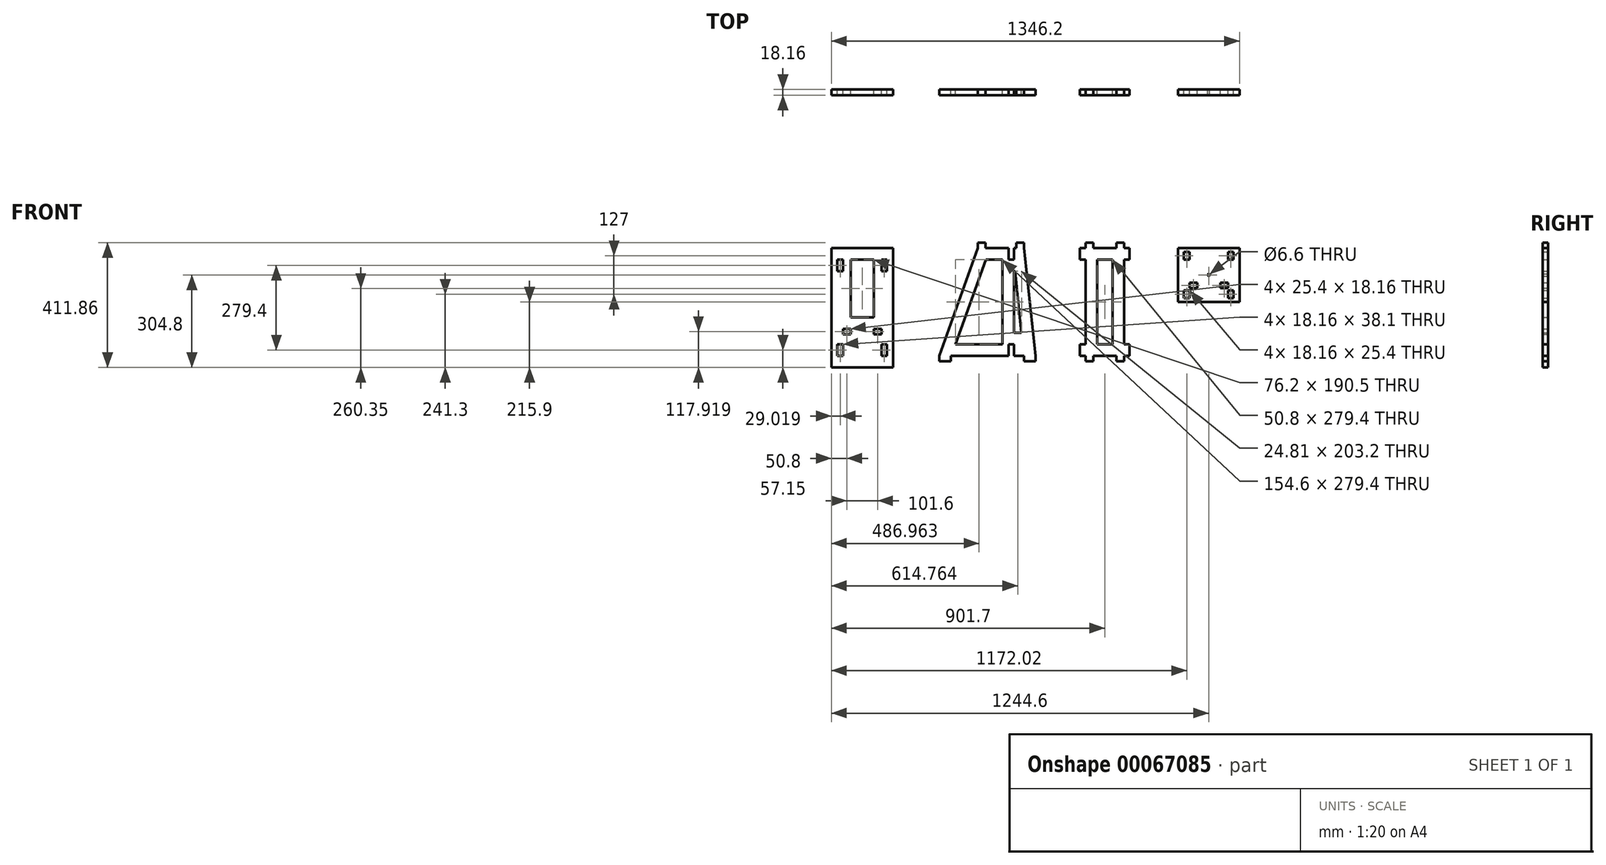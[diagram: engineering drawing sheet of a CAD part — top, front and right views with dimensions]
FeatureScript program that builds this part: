
annotation { "Feature Type Name" : "Feature", "Feature Type Description" : "" }
export const myFeature = defineFeature(function(context is Context, id is Id, definition is map)
    precondition{}
    {
        {
            var Q0;
            Q0=qCreatedBy(makeId("Front.planeOp"),FACE);
            var sketch = newSketch(context, id + "F0", { "sketchPlane" : qUnion([Q0])});
            skLineSegment(sketch, "E0", {"start": v(0, 177.8) * mm, "end": v(0, 139.7) * mm});
            skLineSegment(sketch, "E1.0", {"start": v(18.16, 177.8) * mm, "end": v(18.16, 139.7) * mm});
            skLineSegment(sketch, "E2", {"start": v(0, 177.8) * mm, "end": v(-76.2, 177.8) * mm});
            skLineSegment(sketch, "E3", {"start": v(18.16, 177.8) * mm, "end": v(25.4, 177.8) * mm});
            skLineSegment(sketch, "E4", {"start": v(0, -177.8) * mm, "end": v(-190.5, -177.8) * mm});
            skLineSegment(sketch, "E5", {"start": v(18.16, -177.8) * mm, "end": v(50.8, -177.8) * mm});
            skLineSegment(sketch, "E6", {"start": v(-101.6, 177.8) * mm, "end": v(-228.6, -177.8) * mm});
            skLineSegment(sketch, "E7", {"start": v(50.8, 177.8) * mm, "end": v(88.9, -177.8) * mm});
            skLineSegment(sketch, "E8.0", {"start": v(-19.94, 139.7) * mm, "end": v(-19.94, -139.7) * mm});
            skLineSegment(sketch, "E8.1", {"start": v(-19.94, 139.7) * mm, "end": v(-74.75, 139.7) * mm});
            skLineSegment(sketch, "E8.2", {"start": v(-74.75, 139.7) * mm, "end": v(-174.54, -139.7) * mm});
            skLineSegment(sketch, "E8.3", {"start": v(-19.94, -139.7) * mm, "end": v(-174.54, -139.7) * mm});
            skLineSegment(sketch, "E9", {"start": v(0, 139.7) * mm, "end": v(18.16, 139.7) * mm});
            skLineSegment(sketch, "E10", {"start": v(0, -139.7) * mm, "end": v(18.16, -139.7) * mm});
            skLineSegment(sketch, "E11.top", {"start": v(-101.6, 195.96) * mm, "end": v(-76.2, 195.96) * mm});
            skLineSegment(sketch, "E11.left", {"start": v(-101.6, 177.8) * mm, "end": v(-101.6, 195.96) * mm});
            skLineSegment(sketch, "E11.right", {"start": v(-76.2, 177.8) * mm, "end": v(-76.2, 195.96) * mm});
            skLineSegment(sketch, "E12.top", {"start": v(50.8, 195.96) * mm, "end": v(25.4, 195.96) * mm});
            skLineSegment(sketch, "E12.left", {"start": v(50.8, 177.8) * mm, "end": v(50.8, 195.96) * mm});
            skLineSegment(sketch, "E12.right", {"start": v(25.4, 177.8) * mm, "end": v(25.4, 195.96) * mm});
            skLineSegment(sketch, "E13.top", {"start": v(-228.6, -195.96) * mm, "end": v(-190.5, -195.96) * mm});
            skLineSegment(sketch, "E13.left", {"start": v(-228.6, -177.8) * mm, "end": v(-228.6, -195.96) * mm});
            skLineSegment(sketch, "E13.right", {"start": v(-190.5, -177.8) * mm, "end": v(-190.5, -195.96) * mm});
            skLineSegment(sketch, "E14.top", {"start": v(88.9, -195.96) * mm, "end": v(50.8, -195.96) * mm});
            skLineSegment(sketch, "E14.left", {"start": v(88.9, -177.8) * mm, "end": v(88.9, -195.96) * mm});
            skLineSegment(sketch, "E14.right", {"start": v(50.8, -177.8) * mm, "end": v(50.8, -195.96) * mm});
            skLineSegment(sketch, "E15", {"start": v(0, 139.7) * mm, "end": v(0, -139.7) * mm, "construction": true});
            skLineSegment(sketch, "E16", {"start": v(18.16, 139.7) * mm, "end": v(18.16, -139.7) * mm, "construction": true});
            skLineSegment(sketch, "E17", {"start": v(0, -139.7) * mm, "end": v(0, -177.8) * mm});
            skLineSegment(sketch, "E18", {"start": v(18.16, -139.7) * mm, "end": v(18.16, -177.8) * mm});
            skLineSegment(sketch, "E19.bottom", {"start": v(279.4, 177.8) * mm, "end": v(355.6, 177.8) * mm});
            skLineSegment(sketch, "E19.top", {"start": v(279.4, -177.8) * mm, "end": v(355.6, -177.8) * mm});
            skLineSegment(sketch, "E19.left", {"start": v(254, 139.7) * mm, "end": v(254, -139.7) * mm});
            skLineSegment(sketch, "E19.right", {"start": v(381, 139.7) * mm, "end": v(381, -139.7) * mm});
            skLineSegment(sketch, "E20.bottom", {"start": v(254, 177.8) * mm, "end": v(235.97, 177.8) * mm});
            skLineSegment(sketch, "E20.top", {"start": v(254, 139.7) * mm, "end": v(235.97, 139.7) * mm});
            skLineSegment(sketch, "E20.right", {"start": v(235.97, 177.8) * mm, "end": v(235.97, 139.7) * mm});
            skLineSegment(sketch, "E21", {"start": v(317.5, 177.8) * mm, "end": v(317.5, -177.8) * mm, "construction": true});
            skLineSegment(sketch, "E22", {"start": v(317.5, -177.8) * mm, "end": v(381, 0) * mm, "construction": true});
            skLineSegment(sketch, "E23", {"start": v(381, 0) * mm, "end": v(254, 0) * mm, "construction": true});
            skLineSegment(sketch, "E24.MirrorCS", {"start": v(381, 177.8) * mm, "end": v(399.03, 177.8) * mm});
            skLineSegment(sketch, "E25.MirrorCS", {"start": v(399.03, 177.8) * mm, "end": v(399.03, 139.7) * mm});
            skLineSegment(sketch, "E26.MirrorCS", {"start": v(381, 139.7) * mm, "end": v(399.03, 139.7) * mm});
            skLineSegment(sketch, "E27.MirrorCS", {"start": v(254, -177.8) * mm, "end": v(235.97, -177.8) * mm});
            skLineSegment(sketch, "E28.MirrorCS", {"start": v(381, -139.7) * mm, "end": v(399.03, -139.7) * mm});
            skLineSegment(sketch, "E29.MirrorCS", {"start": v(381, -177.8) * mm, "end": v(399.03, -177.8) * mm});
            skLineSegment(sketch, "E30.MirrorCS", {"start": v(254, -139.7) * mm, "end": v(235.97, -139.7) * mm});
            skLineSegment(sketch, "E31.MirrorCS", {"start": v(235.97, -177.8) * mm, "end": v(235.97, -139.7) * mm});
            skLineSegment(sketch, "E32.MirrorCS", {"start": v(399.03, -177.8) * mm, "end": v(399.03, -139.7) * mm});
            skLineSegment(sketch, "E33.top", {"start": v(254, -195.96) * mm, "end": v(279.4, -195.96) * mm});
            skLineSegment(sketch, "E33.left", {"start": v(254, -177.8) * mm, "end": v(254, -195.96) * mm});
            skLineSegment(sketch, "E33.right", {"start": v(279.4, -177.8) * mm, "end": v(279.4, -195.96) * mm});
            skLineSegment(sketch, "E34.MirrorCS", {"start": v(381, -195.96) * mm, "end": v(355.6, -195.96) * mm});
            skLineSegment(sketch, "E35.MirrorCS", {"start": v(381, -177.8) * mm, "end": v(381, -195.96) * mm});
            skLineSegment(sketch, "E36.MirrorCS", {"start": v(355.6, -177.8) * mm, "end": v(355.6, -195.96) * mm});
            skLineSegment(sketch, "E37.MirrorCS", {"start": v(254, 195.96) * mm, "end": v(279.4, 195.96) * mm});
            skLineSegment(sketch, "E38.MirrorCS", {"start": v(254, 177.8) * mm, "end": v(254, 195.96) * mm});
            skLineSegment(sketch, "E39.MirrorCS", {"start": v(279.4, 177.8) * mm, "end": v(279.4, 195.96) * mm});
            skLineSegment(sketch, "E40.MirrorCS", {"start": v(355.6, 177.8) * mm, "end": v(355.6, 195.96) * mm});
            skLineSegment(sketch, "E41.MirrorCS", {"start": v(381, 177.8) * mm, "end": v(381, 195.96) * mm});
            skLineSegment(sketch, "E42.MirrorCS", {"start": v(381, 195.96) * mm, "end": v(355.6, 195.96) * mm});
            skPoint(sketch, "E43.orphan", {"position": v(381, -177.8) * mm});
            skPoint(sketch, "E44.orphan", {"position": v(381, 177.8) * mm});
            skLineSegment(sketch, "E45.0", {"start": v(292.1, 139.7) * mm, "end": v(342.9, 139.7) * mm});
            skLineSegment(sketch, "E46.0", {"start": v(342.9, 139.7) * mm, "end": v(342.9, -139.7) * mm});
            skLineSegment(sketch, "E47.0", {"start": v(292.1, 139.7) * mm, "end": v(292.1, -139.7) * mm});
            skLineSegment(sketch, "E48.0", {"start": v(292.1, -139.7) * mm, "end": v(342.9, -139.7) * mm});
            skLineSegment(sketch, "E49", {"start": v(22.08, 101.6) * mm, "end": v(42.97, -101.6) * mm});
            skLineSegment(sketch, "E50.0", {"start": v(18.16, 101.6) * mm, "end": v(22.08, 101.6) * mm});
            skLineSegment(sketch, "E51.0", {"start": v(18.16, -101.6) * mm, "end": v(42.97, -101.6) * mm});
            skLineSegment(sketch, "E52", {"start": v(18.16, 101.6) * mm, "end": v(18.16, -101.6) * mm});
            skLineSegment(sketch, "E53.bottom", {"start": v(558.8, 177.8) * mm, "end": v(762, 177.8) * mm});
            skLineSegment(sketch, "E53.top", {"start": v(558.8, 0) * mm, "end": v(762, 0) * mm});
            skLineSegment(sketch, "E53.left", {"start": v(558.8, 177.8) * mm, "end": v(558.8, 0) * mm});
            skLineSegment(sketch, "E53.right", {"start": v(762, 177.8) * mm, "end": v(762, 0) * mm});
            skLineSegment(sketch, "E54", {"start": v(558.8, 88.9) * mm, "end": v(762, 88.9) * mm, "construction": true});
            skLineSegment(sketch, "E55", {"start": v(762, 88.9) * mm, "end": v(660.4, 177.8) * mm, "construction": true});
            skLineSegment(sketch, "E56", {"start": v(660.4, 177.8) * mm, "end": v(660.4, 0) * mm, "construction": true});
            skLineSegment(sketch, "E57.0", {"start": v(596.9, 177.8) * mm, "end": v(596.9, 0) * mm, "construction": true});
            skLineSegment(sketch, "E58.0", {"start": v(723.9, 177.8) * mm, "end": v(723.9, 0) * mm, "construction": true});
            skLineSegment(sketch, "E59.0", {"start": v(558.8, 12.7) * mm, "end": v(762, 12.7) * mm, "construction": true});
            skLineSegment(sketch, "E60.0", {"start": v(558.8, 165.1) * mm, "end": v(762, 165.1) * mm, "construction": true});
            skLineSegment(sketch, "E61.0", {"start": v(558.8, 63.5) * mm, "end": v(762, 63.5) * mm, "construction": true});
            skLineSegment(sketch, "E62.bottom", {"start": v(596.9, 63.5) * mm, "end": v(622.3, 63.5) * mm});
            skLineSegment(sketch, "E62.top", {"start": v(596.9, 45.34) * mm, "end": v(622.3, 45.34) * mm});
            skLineSegment(sketch, "E62.left", {"start": v(596.9, 63.5) * mm, "end": v(596.9, 45.34) * mm});
            skLineSegment(sketch, "E62.right", {"start": v(622.3, 63.5) * mm, "end": v(622.3, 45.34) * mm});
            skLineSegment(sketch, "E63.bottom", {"start": v(596.9, 12.7) * mm, "end": v(578.74, 12.7) * mm});
            skLineSegment(sketch, "E63.top", {"start": v(596.9, 38.1) * mm, "end": v(578.74, 38.1) * mm});
            skLineSegment(sketch, "E63.left", {"start": v(596.9, 12.7) * mm, "end": v(596.9, 38.1) * mm});
            skLineSegment(sketch, "E63.right", {"start": v(578.74, 12.7) * mm, "end": v(578.74, 38.1) * mm});
            skLineSegment(sketch, "E64.MirrorCS", {"start": v(698.5, 63.5) * mm, "end": v(698.5, 45.34) * mm});
            skLineSegment(sketch, "E65.MirrorCS", {"start": v(723.9, 63.5) * mm, "end": v(723.9, 45.34) * mm});
            skLineSegment(sketch, "E66.MirrorCS", {"start": v(723.9, 45.34) * mm, "end": v(698.5, 45.34) * mm});
            skLineSegment(sketch, "E67.MirrorCS", {"start": v(723.9, 12.7) * mm, "end": v(723.9, 38.1) * mm});
            skLineSegment(sketch, "E68.MirrorCS", {"start": v(723.9, 38.1) * mm, "end": v(742.06, 38.1) * mm});
            skLineSegment(sketch, "E69.MirrorCS", {"start": v(723.9, 63.5) * mm, "end": v(698.5, 63.5) * mm});
            skLineSegment(sketch, "E70.MirrorCS", {"start": v(742.06, 12.7) * mm, "end": v(742.06, 38.1) * mm});
            skLineSegment(sketch, "E71.MirrorCS", {"start": v(723.9, 12.7) * mm, "end": v(742.06, 12.7) * mm});
            skLineSegment(sketch, "E72.MirrorCS", {"start": v(596.9, 165.1) * mm, "end": v(596.9, 139.7) * mm});
            skLineSegment(sketch, "E73.MirrorCS", {"start": v(578.74, 165.1) * mm, "end": v(578.74, 139.7) * mm});
            skLineSegment(sketch, "E74.MirrorCS", {"start": v(723.9, 165.1) * mm, "end": v(742.06, 165.1) * mm});
            skLineSegment(sketch, "E75.MirrorCS", {"start": v(596.9, 165.1) * mm, "end": v(578.74, 165.1) * mm});
            skLineSegment(sketch, "E76.MirrorCS", {"start": v(723.9, 165.1) * mm, "end": v(723.9, 139.7) * mm});
            skLineSegment(sketch, "E77.MirrorCS", {"start": v(723.9, 139.7) * mm, "end": v(742.06, 139.7) * mm});
            skLineSegment(sketch, "E78.MirrorCS", {"start": v(742.06, 165.1) * mm, "end": v(742.06, 139.7) * mm});
            skLineSegment(sketch, "E79.MirrorCS", {"start": v(596.9, 139.7) * mm, "end": v(578.74, 139.7) * mm});
            skCircle(sketch, "E80", {"center": v(660.4, 88.9) * mm, "radius": 3.3 * mm});
            skLineSegment(sketch, "E81.bottom", {"start": v(-381, 177.8) * mm, "end": v(-584.2, 177.8) * mm});
            skLineSegment(sketch, "E81.top", {"start": v(-381, -215.9) * mm, "end": v(-584.2, -215.9) * mm});
            skLineSegment(sketch, "E81.left", {"start": v(-381, 177.8) * mm, "end": v(-381, -215.9) * mm});
            skLineSegment(sketch, "E81.right", {"start": v(-584.2, 177.8) * mm, "end": v(-584.2, -215.9) * mm});
            skLineSegment(sketch, "E82", {"start": v(-584.2, -19.05) * mm, "end": v(-381, -19.05) * mm, "construction": true});
            skLineSegment(sketch, "E83", {"start": v(-381, -19.05) * mm, "end": v(-482.6, 177.8) * mm, "construction": true});
            skLineSegment(sketch, "E84", {"start": v(-482.6, 177.8) * mm, "end": v(-482.6, -215.9) * mm, "construction": true});
            skLineSegment(sketch, "E85.0", {"start": v(-584.2, 139.7) * mm, "end": v(-381, 139.7) * mm, "construction": true});
            skLineSegment(sketch, "E86.0", {"start": v(-584.2, -177.8) * mm, "end": v(-381, -177.8) * mm, "construction": true});
            skLineSegment(sketch, "E87.0", {"start": v(-546.1, 177.8) * mm, "end": v(-546.1, -215.9) * mm, "construction": true});
            skLineSegment(sketch, "E88.0", {"start": v(-419.1, 177.8) * mm, "end": v(-419.1, -215.9) * mm, "construction": true});
            skLineSegment(sketch, "E89.0", {"start": v(-584.2, -88.9) * mm, "end": v(-381, -88.9) * mm, "construction": true});
            skLineSegment(sketch, "E90.bottom", {"start": v(-546.1, 139.7) * mm, "end": v(-564.26, 139.7) * mm});
            skLineSegment(sketch, "E90.top", {"start": v(-546.1, 101.6) * mm, "end": v(-564.26, 101.6) * mm});
            skLineSegment(sketch, "E90.left", {"start": v(-546.1, 139.7) * mm, "end": v(-546.1, 101.6) * mm});
            skLineSegment(sketch, "E90.right", {"start": v(-564.26, 139.7) * mm, "end": v(-564.26, 101.6) * mm});
            skLineSegment(sketch, "E91.bottom", {"start": v(-546.1, -88.9) * mm, "end": v(-520.7, -88.9) * mm});
            skLineSegment(sketch, "E91.top", {"start": v(-546.1, -107.06) * mm, "end": v(-520.7, -107.06) * mm});
            skLineSegment(sketch, "E91.left", {"start": v(-546.1, -88.9) * mm, "end": v(-546.1, -107.06) * mm});
            skLineSegment(sketch, "E91.right", {"start": v(-520.7, -88.9) * mm, "end": v(-520.7, -107.06) * mm});
            skLineSegment(sketch, "E92.MirrorCS", {"start": v(-419.1, 139.7) * mm, "end": v(-419.1, 101.6) * mm});
            skLineSegment(sketch, "E93.MirrorCS", {"start": v(-419.1, 101.6) * mm, "end": v(-400.94, 101.6) * mm});
            skLineSegment(sketch, "E94.MirrorCS", {"start": v(-400.94, 139.7) * mm, "end": v(-400.94, 101.6) * mm});
            skLineSegment(sketch, "E95.MirrorCS", {"start": v(-419.1, 139.7) * mm, "end": v(-400.94, 139.7) * mm});
            skLineSegment(sketch, "E96.MirrorCS", {"start": v(-546.1, -139.7) * mm, "end": v(-564.26, -139.7) * mm});
            skLineSegment(sketch, "E97.MirrorCS", {"start": v(-546.1, -177.8) * mm, "end": v(-564.26, -177.8) * mm});
            skLineSegment(sketch, "E98.MirrorCS", {"start": v(-419.1, -177.8) * mm, "end": v(-400.94, -177.8) * mm});
            skLineSegment(sketch, "E99.MirrorCS", {"start": v(-419.1, -139.7) * mm, "end": v(-400.94, -139.7) * mm});
            skLineSegment(sketch, "E100.MirrorCS", {"start": v(-564.26, -177.8) * mm, "end": v(-564.26, -139.7) * mm});
            skLineSegment(sketch, "E101.MirrorCS", {"start": v(-546.1, -177.8) * mm, "end": v(-546.1, -139.7) * mm});
            skLineSegment(sketch, "E102.MirrorCS", {"start": v(-400.94, -177.8) * mm, "end": v(-400.94, -139.7) * mm});
            skLineSegment(sketch, "E103.MirrorCS", {"start": v(-419.1, -177.8) * mm, "end": v(-419.1, -139.7) * mm});
            skLineSegment(sketch, "E104.MirrorCS", {"start": v(-419.1, -107.06) * mm, "end": v(-444.5, -107.06) * mm});
            skLineSegment(sketch, "E105.MirrorCS", {"start": v(-444.5, -88.9) * mm, "end": v(-444.5, -107.06) * mm});
            skLineSegment(sketch, "E106.MirrorCS", {"start": v(-419.1, -88.9) * mm, "end": v(-444.5, -88.9) * mm});
            skLineSegment(sketch, "E107.MirrorCS", {"start": v(-419.1, -88.9) * mm, "end": v(-419.1, -107.06) * mm});
            skLineSegment(sketch, "E108.trimOffspring", {"start": v(-520.7, 139.7) * mm, "end": v(-520.7, -50.8) * mm});
            skLineSegment(sketch, "E109.trimOffspring", {"start": v(-520.7, 139.7) * mm, "end": v(-444.5, 139.7) * mm});
            skLineSegment(sketch, "E110.trimOffspring", {"start": v(-444.5, 139.7) * mm, "end": v(-444.5, -50.8) * mm});
            skLineSegment(sketch, "E111.trimOffspring", {"start": v(-520.7, -50.8) * mm, "end": v(-444.5, -50.8) * mm});
            skSolve(sketch);
        }
        {
            var Q0;
            Q0=makeQuery(id+"F0.imprint","IMPRINT",FACE,{"disambiguationData":[TD([[makeQuery(id+"F0.imprint","IMPRINT",EDGE,{"derivedFrom":sQuery(id+"F0.wireOp",EDGE,"E0")}),-1.0]])]});
            var Q1;
            Q1=makeQuery(id+"F0.imprint","IMPRINT",FACE,{"disambiguationData":[TD([[makeQuery(id+"F0.imprint","IMPRINT",EDGE,{"derivedFrom":sQuery(id+"F0.wireOp",EDGE,"E19.bottom")}),-1.0]])]});
            var Q2;
            Q2=makeQuery(id+"F0.imprint","IMPRINT",FACE,{"disambiguationData":[TD([[makeQuery(id+"F0.imprint","IMPRINT",EDGE,{"derivedFrom":sQuery(id+"F0.wireOp",EDGE,"E53.bottom")}),-1.0]])]});
            var Q3;
            Q3=makeQuery(id+"F0.imprint","IMPRINT",FACE,{"disambiguationData":[TD([[makeQuery(id+"F0.imprint","IMPRINT",EDGE,{"derivedFrom":sQuery(id+"F0.wireOp",EDGE,"E81.bottom")}),1.0]])]});
            extrude(context, id + "F1", {"entities" : qUnion([Q0, Q1, Q2, Q3]), "depth" : 18.16 * mm});
        }
    });
